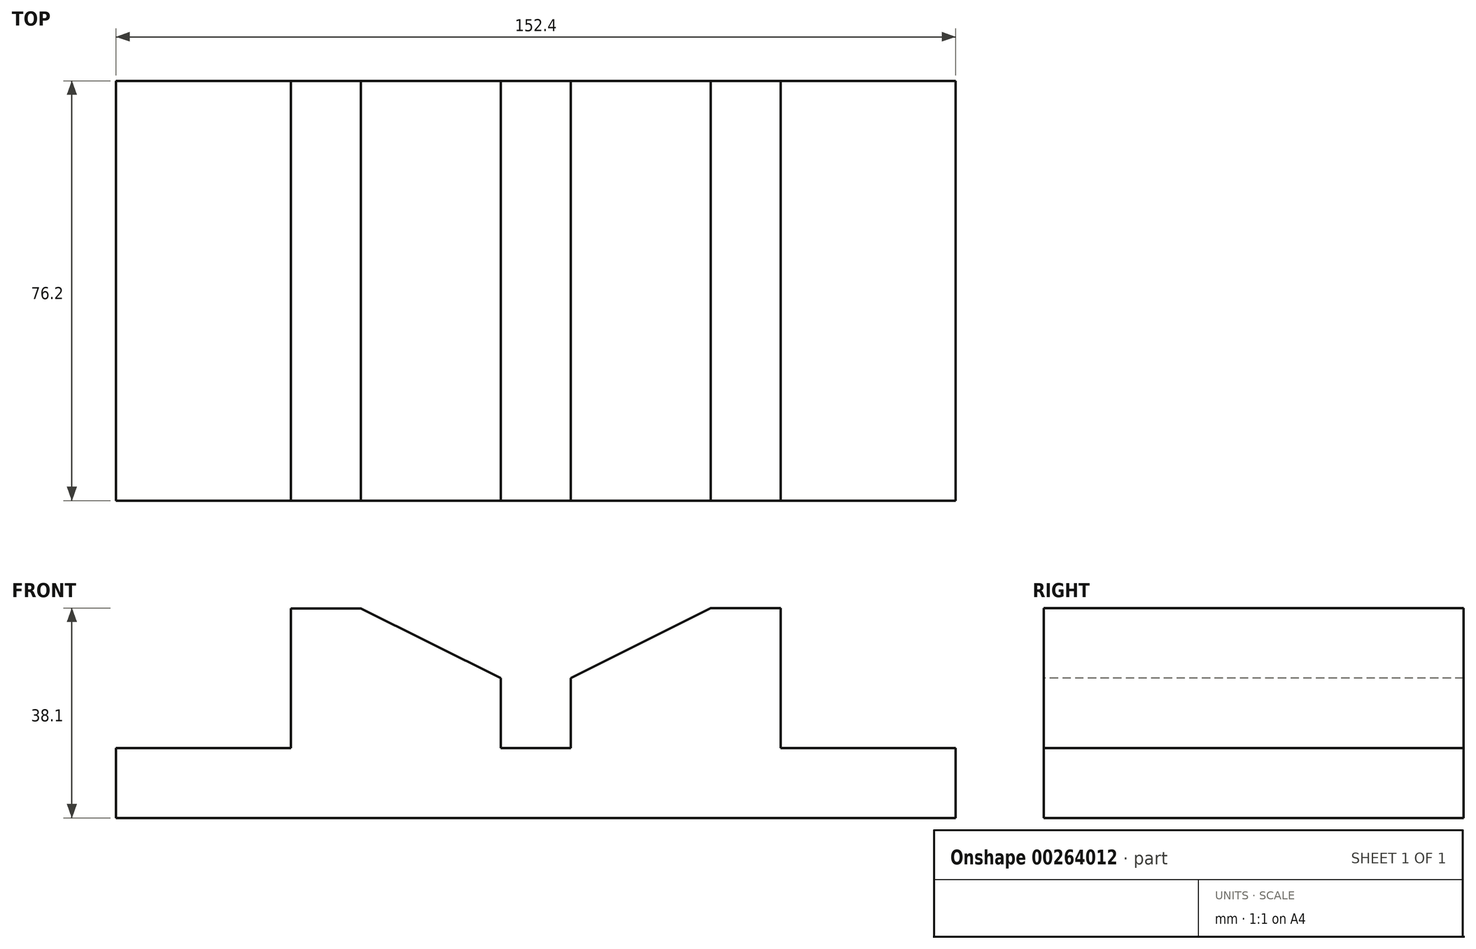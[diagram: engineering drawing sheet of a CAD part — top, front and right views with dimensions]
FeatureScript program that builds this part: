
annotation { "Feature Type Name" : "Feature", "Feature Type Description" : "" }
export const myFeature = defineFeature(function(context is Context, id is Id, definition is map)
    precondition{}
    {
        {
            var Q0;
            Q0=qCreatedBy(makeId("Front.planeOp"),FACE);
            var sketch = newSketch(context, id + "F0", { "sketchPlane" : qUnion([Q0])});
            skLineSegment(sketch, "E0", {"start": v(0, -75.75) * mm, "end": v(-76.2, -75.75) * mm});
            skLineSegment(sketch, "E1", {"start": v(-76.2, -75.75) * mm, "end": v(76.2, -75.75) * mm});
            skLineSegment(sketch, "E2", {"start": v(-76.2, -75.75) * mm, "end": v(-76.2, -63.05) * mm});
            skLineSegment(sketch, "E3", {"start": v(76.2, -75.75) * mm, "end": v(76.2, -63.05) * mm});
            skLineSegment(sketch, "E4", {"start": v(76.2, -63.05) * mm, "end": v(-76.2, -63.05) * mm});
            skLineSegment(sketch, "E5", {"start": v(-76.2, -63.05) * mm, "end": v(-44.45, -63.05) * mm});
            skLineSegment(sketch, "E6", {"start": v(-44.45, -63.05) * mm, "end": v(-44.45, -37.77) * mm});
            skLineSegment(sketch, "E7", {"start": v(-44.45, -37.77) * mm, "end": v(-31.75, -37.77) * mm});
            skLineSegment(sketch, "E8", {"start": v(76.2, -63.05) * mm, "end": v(44.45, -63.05) * mm});
            skLineSegment(sketch, "E9", {"start": v(44.45, -63.05) * mm, "end": v(44.45, -37.65) * mm});
            skLineSegment(sketch, "E10", {"start": v(44.45, -37.65) * mm, "end": v(31.75, -37.65) * mm});
            skLineSegment(sketch, "E11", {"start": v(-44.45, -63.05) * mm, "end": v(-6.35, -63.05) * mm});
            skLineSegment(sketch, "E12", {"start": v(44.45, -63.05) * mm, "end": v(6.35, -63.05) * mm});
            skLineSegment(sketch, "E13", {"start": v(6.35, -63.05) * mm, "end": v(6.35, -50.35) * mm});
            skLineSegment(sketch, "E14", {"start": v(-6.35, -50.35) * mm, "end": v(-6.35, -63.05) * mm});
            skLineSegment(sketch, "E15", {"start": v(31.75, -37.65) * mm, "end": v(6.35, -50.35) * mm});
            skLineSegment(sketch, "E16", {"start": v(-31.75, -37.77) * mm, "end": v(-6.35, -50.35) * mm});
            skSolve(sketch);
        }
        {
            var Q0;
            Q0=makeQuery(id+"F0.imprint","IMPRINT",FACE,{"disambiguationData":[TD([[makeQuery(id+"F0.imprint","IMPRINT",EDGE,{"derivedFrom":sQuery(id+"F0.wireOp",EDGE,"E9")}),1.0]])]});
            var Q1;
            Q1=makeQuery(id+"F0.imprint","IMPRINT",FACE,{"disambiguationData":[TD([[makeQuery(id+"F0.imprint","IMPRINT",EDGE,{"derivedFrom":sQuery(id+"F0.wireOp",EDGE,"E6")}),-1.0]])]});
            var Q2;
            {var subQ1=sQuery(id+"F0.wireOp",EDGE,"E2");Q2=makeQuery(id+"F0.imprint","IMPRINT",FACE,{"disambiguationData":[TD([[makeQuery(id+"F0.imprint","IMPRINT",EDGE,{"derivedFrom":subQ1}),-1.0]])]});}
            extrude(context, id + "F1", {"entities" : qUnion([Q0, Q1, Q2]), "oppositeDirection" : true, "depth" : 76.2 * mm});
        }
    });
